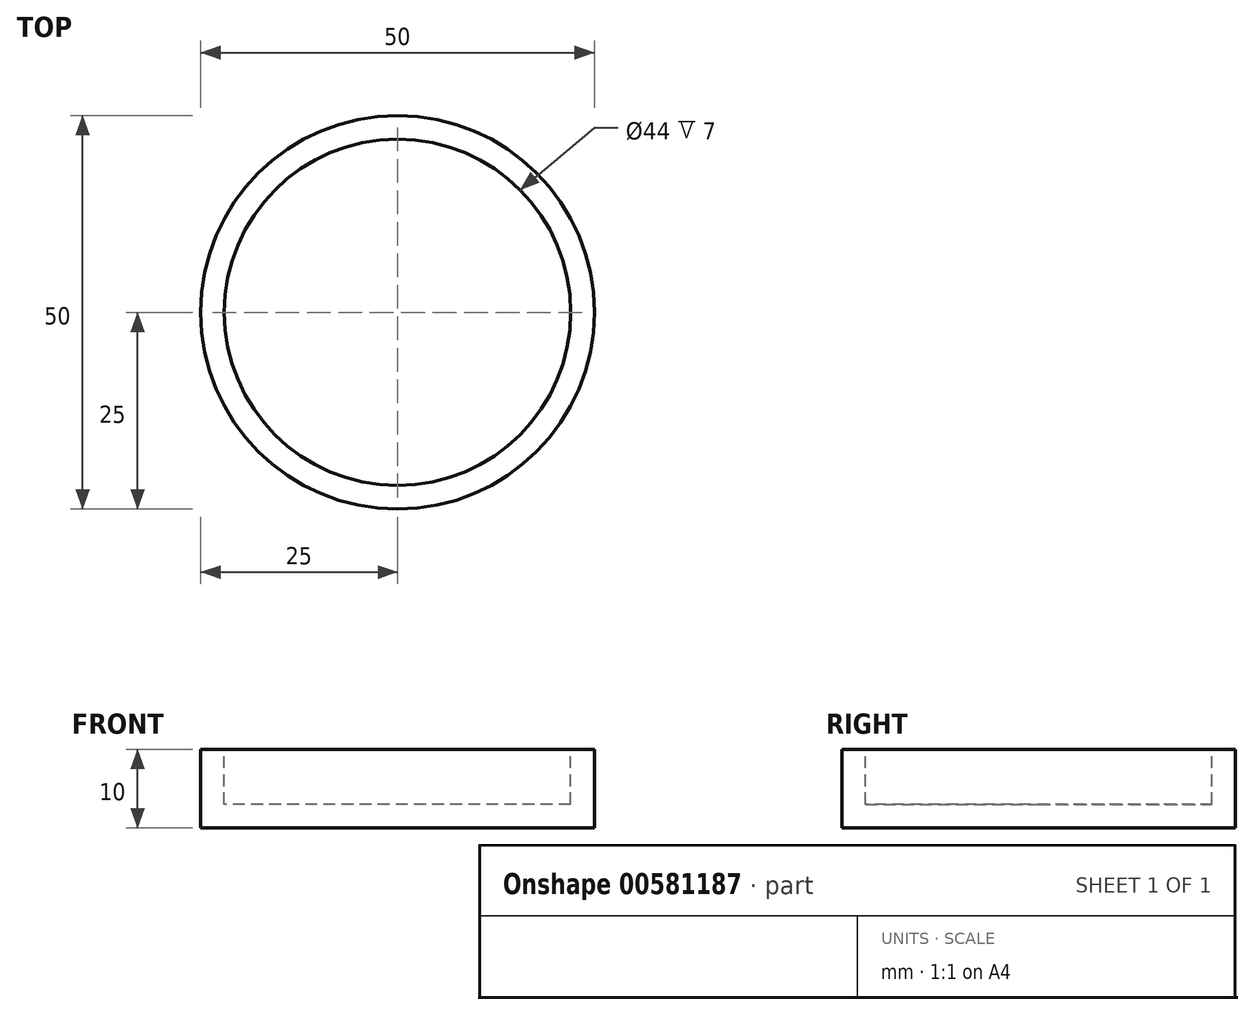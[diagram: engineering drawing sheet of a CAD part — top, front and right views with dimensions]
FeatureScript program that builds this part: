
annotation { "Feature Type Name" : "Feature", "Feature Type Description" : "" }
export const myFeature = defineFeature(function(context is Context, id is Id, definition is map)
    precondition{}
    {
        {
            var Q0;
            Q0=qCreatedBy(makeId("Front.planeOp"),FACE);
            var sketch = newSketch(context, id + "F0", { "sketchPlane" : qUnion([Q0])});
            skLineSegment(sketch, "E0.bottom", {"start": v(0, 0) * mm, "end": v(-25, 0) * mm});
            skLineSegment(sketch, "E0.right", {"start": v(-25, 0) * mm, "end": v(-25, 10) * mm});
            skPoint(sketch, "E0.middle", {"position": v(0, 5) * mm});
            skLineSegment(sketch, "E1.top", {"start": v(-22, 3) * mm, "end": v(0, 3) * mm});
            skLineSegment(sketch, "E1.left", {"start": v(-22, 10) * mm, "end": v(-22, 3) * mm});
            skLineSegment(sketch, "E2.trimOffspring", {"start": v(-22, 10) * mm, "end": v(-25, 10) * mm});
            skLineSegment(sketch, "E3", {"start": v(0, 3) * mm, "end": v(0, 0) * mm});
            skLineSegment(sketch, "E4", {"start": v(0, 39.75) * mm, "end": v(0, -38.76) * mm, "construction": true});
            skSolve(sketch);
        }
        {
            var Q0;
            Q0=makeQuery(id+"F0.imprint","IMPRINT",FACE,{"disambiguationData":[TD([[makeQuery(id+"F0.imprint","IMPRINT",EDGE,{"derivedFrom":sQuery(id+"F0.wireOp",EDGE,"E0.bottom")}),-1.0]])]});
            var Q1;
            Q1=sQuery(id+"F0.wireOp",EDGE,"E4");
            revolve(context, id + "F1", {"entities" : qUnion([Q0]), "axis" : qUnion([Q1]), "revolveType" : RevolveType.FULL});
        }
    });
